# Revit family: B279EN
name_source: partatom
category: Mechanical Equipment
units: mm (PartAtom-declared; Revit-internal decimal feet)

## family parameters
Always vertical = Yes
Cut with Voids When Loaded = No
OmniClass Number = 23.75.00.00
OmniClass Title = Climate Control (HVAC)
Part Type = Normal
Room Calculation Point = No
Round Connector Dimension = Use Diameter
Shared = No
Work Plane-Based = No

## types (4) — shared parameters
00_20_Manufacturer = Blauberg
00_20_Name = Air handling unit
Air Flow (default) = 0.0 m³/h
Casing Material = Polypropylene (black)
Filter = G4 / Coarse > 60%
Frequency = 60 Hz
H = 880 mm  [stored 2.88714 ft]
H1 = 939 mm  [stored 3.08071 ft]
L = 616 mm  [stored 2.021 ft]
L1 = 230 mm
Load Classification = HVAC
Maintenance zone material = <By Category>
Maximum Air Flow = 410.0 m³/h
Number of Fase = 1
Pressure_Static_Air = 0.0 Pa
Sound pressure level at 3 m distance = 26 dBA
Voltage = 230 V
W = 782 mm
W1 = 355 mm  [stored 1.1647 ft]
Weight = 26.00 kg
zero-valued in all types: Default Elevation

## per-type parameters (varying)
| type | 00_20_Type | Amperage | Power |
| Reneo S 350/351 R | Reneo S 350/351 | 2 A | 213 W |
| Reneo S 350/351-E | Reneo S 350/351-E | 2 A | 213 W |
| Reneo SE 350/351 | Reneo SE 350/351 | 6 A | 1263 W |
| Reneo SE 350/351-E | Reneo SE 350/351-E | 6 A | 1263 W |

note: [stored X ft] marks values corroborated as IEEE doubles in the binary element streams (Revit-internal decimal feet)

## geometry (parser evidence)
native form markers: Sweep x17
no freeform markers — native parametric forms only
